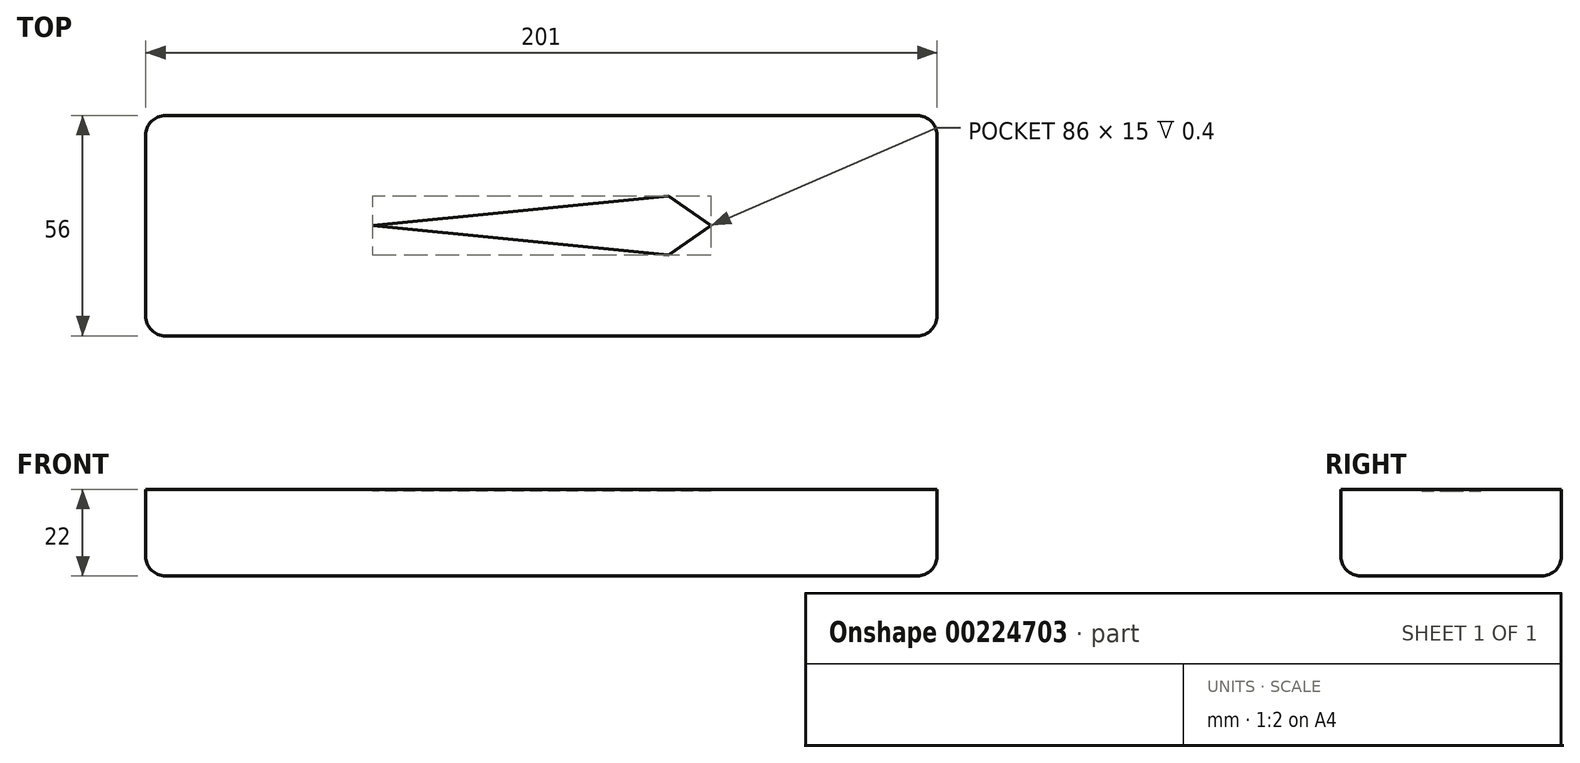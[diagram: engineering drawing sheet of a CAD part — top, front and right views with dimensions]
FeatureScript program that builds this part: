
annotation { "Feature Type Name" : "Feature", "Feature Type Description" : "" }
export const myFeature = defineFeature(function(context is Context, id is Id, definition is map)
    precondition{}
    {
        {
            var Q0;
            Q0=qCreatedBy(makeId("Top.planeOp"),FACE);
            var sketch = newSketch(context, id + "F0", { "sketchPlane" : qUnion([Q0])});
            skLineSegment(sketch, "E0.top", {"start": v(-65.59, 26.14) * mm, "end": v(135.41, 26.14) * mm});
            skLineSegment(sketch, "E0.left", {"start": v(-65.59, -29.86) * mm, "end": v(-65.59, 26.14) * mm});
            skLineSegment(sketch, "E0.right", {"start": v(135.41, -29.86) * mm, "end": v(135.41, 26.14) * mm});
            skLineSegment(sketch, "E1.bottom", {"start": v(-94.22, 101.1) * mm, "end": v(-8.22, 101.1) * mm});
            skLineSegment(sketch, "E1.top", {"start": v(-94.22, 86.1) * mm, "end": v(-8.22, 86.1) * mm});
            skLineSegment(sketch, "E1.left", {"start": v(-94.22, 101.1) * mm, "end": v(-94.22, 86.1) * mm});
            skLineSegment(sketch, "E1.right", {"start": v(-8.22, 101.1) * mm, "end": v(-8.22, 86.1) * mm});
            skLineSegment(sketch, "E2", {"start": v(-94.22, 93.6) * mm, "end": v(-18.97, 93.6) * mm});
            skLineSegment(sketch, "E3", {"start": v(-18.97, 93.6) * mm, "end": v(-8.22, 93.6) * mm});
            skLineSegment(sketch, "E4", {"start": v(-18.97, 93.6) * mm, "end": v(-18.97, 101.1) * mm});
            skLineSegment(sketch, "E5", {"start": v(-18.97, 101.1) * mm, "end": v(-18.97, 93.6) * mm});
            skLineSegment(sketch, "E6", {"start": v(-18.97, 93.6) * mm, "end": v(-18.97, 86.1) * mm});
            skLineSegment(sketch, "E7", {"start": v(-7.98, -1.8) * mm, "end": v(67.27, 5.7) * mm});
            skLineSegment(sketch, "E8", {"start": v(78.02, -1.8) * mm, "end": v(67.27, 5.7) * mm});
            skLineSegment(sketch, "E9", {"start": v(78.02, -1.8) * mm, "end": v(67.27, -9.3) * mm});
            skLineSegment(sketch, "E10", {"start": v(67.27, -9.3) * mm, "end": v(-7.98, -1.8) * mm});
            skPoint(sketch, "E11.start.orphan", {"position": v(34.91, 26.14) * mm});
            skPoint(sketch, "E12.trimOffspring.end.orphan", {"position": v(34.91, -29.86) * mm});
            skPoint(sketch, "E13.trimOffspring.end.orphan", {"position": v(135.41, -1.86) * mm});
            skPoint(sketch, "E14.start.orphan", {"position": v(-65.59, -1.86) * mm});
            skLineSegment(sketch, "E15", {"start": v(-65.59, -29.86) * mm, "end": v(135.41, -29.86) * mm});
            skSolve(sketch);
        }
        {
            var Q0;
            Q0=makeQuery(id+"F0.imprint","IMPRINT",FACE,{"disambiguationData":[TD([[makeQuery(id+"F0.imprint","IMPRINT",EDGE,{"derivedFrom":sQuery(id+"F0.wireOp",EDGE,"E0.top")}),-1.0]])]});
            extrude(context, id + "F1", {"entities" : qUnion([Q0]), "depth" : 22 * mm});
        }
        {
            var Q0;
            Q0=makeQuery(id+"F1.opExtrude","CAP_EDGE",EDGE,{"disambiguationData":[OSD([sQuery(id+"F0.wireOp",EDGE,"E0.top")])],"isStart":true});
            var Q1;
            Q1=makeQuery(id+"F1.opExtrude","CAP_EDGE",EDGE,{"disambiguationData":[OSD([sQuery(id+"F0.wireOp",EDGE,"E0.left")])],"isStart":true});
            var Q2;
            Q2=makeQuery(id+"F1.opExtrude","CAP_EDGE",EDGE,{"disambiguationData":[OSD([sQuery(id+"F0.wireOp",EDGE,"E15")])],"isStart":true});
            var Q3;
            Q3=makeQuery(id+"F1.opExtrude","CAP_EDGE",EDGE,{"disambiguationData":[OSD([sQuery(id+"F0.wireOp",EDGE,"E0.right")])],"isStart":true});
            var Q4;
            Q4=makeQuery(id+"F1.opExtrude","SWEPT_EDGE",EDGE,{"disambiguationData":[OSD([sQuery(id+"F0.wireOp",EDGE,"E0.top"),sQuery(id+"F0.wireOp",EDGE,"E0.right")])]});
            var Q5;
            Q5=makeQuery(id+"F1.opExtrude","SWEPT_EDGE",EDGE,{"disambiguationData":[OSD([sQuery(id+"F0.wireOp",EDGE,"E0.top"),sQuery(id+"F0.wireOp",EDGE,"E0.left")])]});
            var Q6;
            Q6=makeQuery(id+"F1.opExtrude","SWEPT_EDGE",EDGE,{"disambiguationData":[OSD([sQuery(id+"F0.wireOp",EDGE,"E0.left"),sQuery(id+"F0.wireOp",EDGE,"E15")])]});
            var Q7;
            Q7=makeQuery(id+"F1.opExtrude","SWEPT_EDGE",EDGE,{"disambiguationData":[OSD([sQuery(id+"F0.wireOp",EDGE,"E0.right"),sQuery(id+"F0.wireOp",EDGE,"E15")])]});
            fillet(context, id + "F2", {"entities" : qUnion([Q0, Q1, Q2, Q3, Q4, Q5, Q6, Q7]), "radius" : 5 * mm, "tangentPropagation" : true, "allowEdgeOverflow" : false});
        }
        {
            var Q0;
            Q0=makeQuery(id+"F0.imprint","IMPRINT",FACE,{"disambiguationData":[TD([[makeQuery(id+"F0.imprint","IMPRINT",EDGE,{"derivedFrom":sQuery(id+"F0.wireOp",EDGE,"E7")}),-1.0]])]});
            extrude(context, id + "F3", {"entities" : qUnion([Q0]), "operationType" : NewBodyOperationType.ADD, "depth" : 21.6 * mm});
        }
    });
